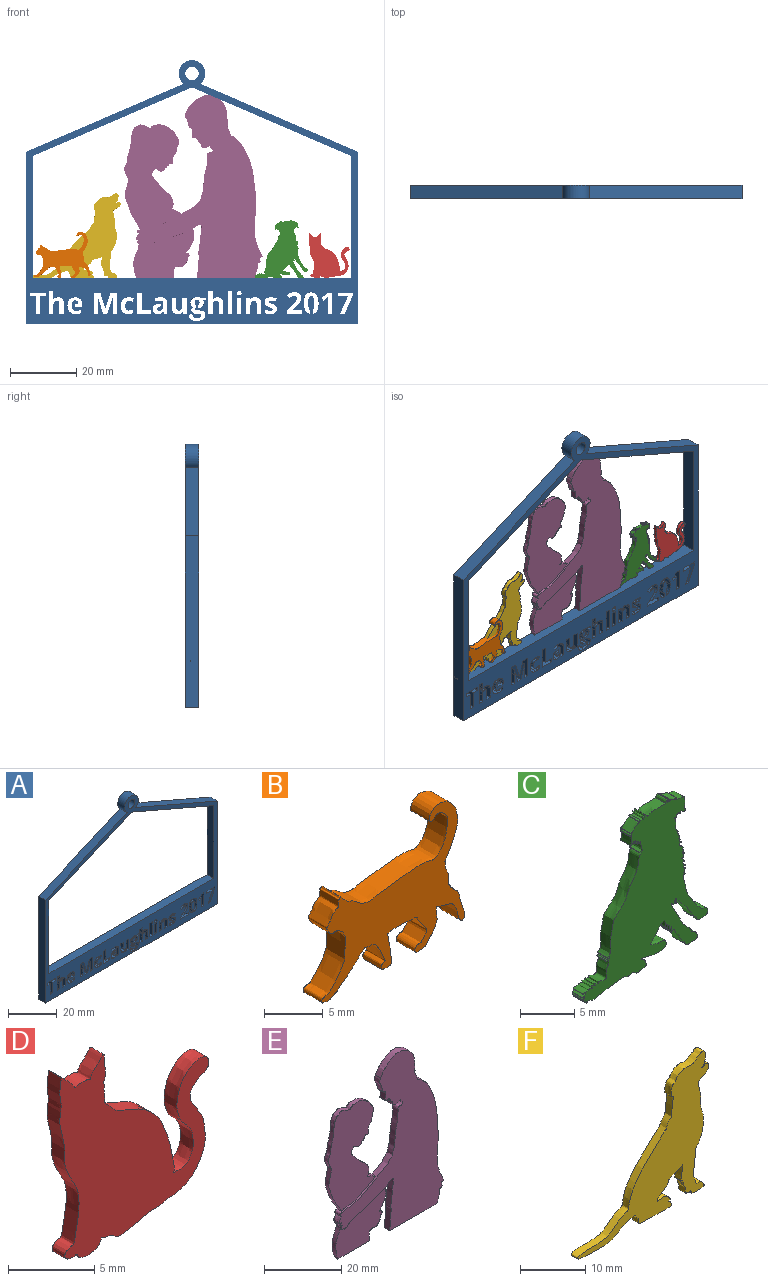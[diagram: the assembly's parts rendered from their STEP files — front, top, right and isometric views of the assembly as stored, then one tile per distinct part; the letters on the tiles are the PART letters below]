
ASSEMBLY  parts=6 mates=6
PART A: 327 faces, bbox 100x4x79.4 mm
  f0: extruded ~4x1.22mm, area 5.9mm2, adj f7,f8,f241,f326
  f1: extruded ~4x1.27mm, area 5.5mm2, adj f7,f8,f250,f316
  f2: plane 4x0.02mm, normal (0.11,0,0.99), area 0.1mm2, adj f7,f8,f251,f315
  f3: extruded ~4x0.02mm, area 0.1mm2, adj f7,f8,f261,f307
  f4: extruded ~4x0.17mm, area 0.9mm2, adj f7,f8,f260,f308
  f5: plane 4x0.02mm, normal (0.03,0,-1), area 0.1mm2, adj f7,f8,f133,f296
  f6: plane 4x2.38mm, normal (0,0,1), area 9.5mm2, adj f7,f8,f114,f287
  f7: plane 100x79.38mm, normal (0,-1,0), area 1515.6mm2, adj f0,f1,f2,f3,f4,f5,f6,f9
  f8: plane 100x79.38mm, normal (0,1,0), area 1515.6mm2, adj f0,f1,f2,f3,f4,f5,f6,f9
  f9: plane 36.69x4mm, normal (-1,0,0), area 146.7mm2, adj f7,f8,f10,f19
  f10: plane 96x4mm, normal (0,0,1), area 384mm2, adj f7,f8,f9,f11
  f11: plane 36.69x4mm, normal (1,0,0), area 146.7mm2, adj f7,f8,f10,f12
  f12: plane 48x20.72mm, normal (0.4,0,-0.92), area 209.1mm2, adj f7,f8,f11,f19
  f13: plane 47.47x20.48mm, normal (0.4,0,0.92), area 206.8mm2, adj f7,f8,f14,f18
  f14: cylinder r=4mm len=8mm, axis (0,1,0), area 78.6mm2, adj f7,f8,f13,f15
  f15: plane 47.47x20.48mm, normal (-0.4,0,0.92), area 206.8mm2, adj f7,f8,f14,f16
  f16: plane 51.8x4mm, normal (-1,0,0), area 207.2mm2, adj f7,f8,f15,f20
  f17: cylinder r=2mm len=4mm, axis (0,1,0), area 50.3mm2, adj f7,f8
  f18: plane 51.8x4mm, normal (1,0,0), area 207.2mm2, adj f7,f8,f13,f20
  f19: plane 48x20.72mm, normal (-0.4,0,-0.92), area 209.1mm2, adj f7,f8,f9,f12
  f20: plane 100x4mm, normal (0,0,-1), area 400mm2, adj f7,f8,f16,f18
  f21: plane 4x1.33mm, normal (0,0,1), area 5.3mm2, adj f7,f8,f22,f24
  f22: plane 4.89x4mm, normal (-1,0,0), area 19.6mm2, adj f7,f8,f21,f23
  f23: plane 4x1.33mm, normal (0,0,-1), area 5.3mm2, adj f7,f8,f22,f24
  f24: plane 4.89x4mm, normal (1,0,0), area 19.6mm2, adj f7,f8,f21,f23
  f25: plane 4x1.33mm, normal (0,0,1), area 5.3mm2, adj f7,f8,f26,f41
  f26: plane 4x3.19mm, normal (-1,0,0), area 12.8mm2, adj f7,f8,f25,f27
  f27: extruded ~4x1.33mm, area 5.8mm2, adj f7,f8,f26,f28
  f28: extruded ~4x1.3mm, area 5.7mm2, adj f7,f8,f27,f29
  f29: extruded ~4x0.89mm, area 3.7mm2, adj f7,f8,f28,f30
  f30: extruded ~4x0.62mm, area 3.3mm2, adj f7,f8,f29,f31
  f31: plane 4x0.07mm, normal (0,0,-1), area 0.3mm2, adj f7,f8,f30,f32
  f32: plane 4x0.63mm, normal (-0.96,0,-0.28), area 2.6mm2, adj f7,f8,f31,f33
  f33: plane 4x1.02mm, normal (0,0,-1), area 4.1mm2, adj f7,f8,f32,f34
  f34: plane 4.89x4mm, normal (1,0,0), area 19.6mm2, adj f7,f8,f33,f35
  f35: plane 4x1.33mm, normal (0,0,1), area 5.3mm2, adj f7,f8,f34,f36
  f36: plane 4x2.3mm, normal (-1,0,0), area 9.2mm2, adj f7,f8,f35,f37
  f37: extruded ~4x1.24mm, area 5.1mm2, adj f7,f8,f36,f38
  f38: extruded ~4x0.81mm, area 3.7mm2, adj f7,f8,f37,f39
  f39: extruded ~4x0.6mm, area 2.7mm2, adj f7,f8,f38,f40
  f40: extruded ~4x0.79mm, area 3.3mm2, adj f7,f8,f39,f41
  f41: plane 4x2.86mm, normal (1,0,0), area 11.4mm2, adj f7,f8,f25,f40
  f42: extruded ~4x1.15mm, area 5.2mm2, adj f7,f8,f43,f67
  f43: extruded ~4x0.63mm, area 2.6mm2, adj f7,f8,f42,f44
  f44: extruded ~4x0.46mm, area 2.5mm2, adj f7,f8,f43,f45
  f45: extruded ~4x0.84mm, area 3.8mm2, adj f7,f8,f44,f46
  f46: extruded ~4x0.83mm, area 3.7mm2, adj f7,f8,f45,f47
  f47: extruded ~4x0.31mm, area 1.5mm2, adj f7,f8,f46,f48
  f48: extruded ~4x0.59mm, area 3mm2, adj f7,f8,f47,f49
  f49: extruded ~4x0.65mm, area 2.7mm2, adj f7,f8,f48,f50
  f50: extruded ~4x0.69mm, area 2.9mm2, adj f7,f8,f49,f51
  f51: plane 4x0.96mm, normal (-0.92,0,0.39), area 4.2mm2, adj f7,f8,f50,f52
  f52: extruded ~4x1.72mm, area 7.1mm2, adj f7,f8,f51,f53
  f53: extruded ~4x1.43mm, area 6mm2, adj f7,f8,f52,f54
  f54: extruded ~4x1.01mm, area 4.7mm2, adj f7,f8,f53,f55
  f55: extruded ~4x0.64mm, area 2.6mm2, adj f7,f8,f54,f56
  f56: extruded ~4x0.46mm, area 2.4mm2, adj f7,f8,f55,f57
  f57: extruded ~4x0.83mm, area 3.8mm2, adj f7,f8,f56,f58
  f58: extruded ~4x0.63mm, area 2.8mm2, adj f7,f8,f57,f59
  f59: extruded ~4x0.33mm, area 1.6mm2, adj f7,f8,f58,f60
  f60: extruded ~4x0.26mm, area 1.1mm2, adj f7,f8,f59,f61
  f61: extruded ~4x0.73mm, area 3.8mm2, adj f7,f8,f60,f62
  f62: extruded ~4x0.82mm, area 3.3mm2, adj f7,f8,f61,f63
  f63: extruded ~4x0.84mm, area 3.6mm2, adj f7,f8,f62,f64
  f64: plane 4x1.1mm, normal (1,0,0), area 4.4mm2, adj f7,f8,f63,f65
  f65: extruded ~4x0.7mm, area 2.9mm2, adj f7,f8,f64,f66
  f66: extruded ~4x0.91mm, area 3.7mm2, adj f7,f8,f65,f67
  f67: extruded ~4x1.57mm, area 6.6mm2, adj f7,f8,f42,f66
  f68: plane 4.47x4mm, normal (0,0,1), area 17.9mm2, adj f7,f8,f69,f91
  f69: plane 4x1.14mm, normal (-1,0,0), area 4.6mm2, adj f7,f8,f68,f70
  f70: plane 4x2.79mm, normal (0,0,-1), area 11.2mm2, adj f7,f8,f69,f71
  f71: plane 4x0.06mm, normal (-1,0,0), area 0.2mm2, adj f7,f8,f70,f72
  f72: plane 4x0.82mm, normal (-0.69,0,0.73), area 4.5mm2, adj f7,f8,f71,f73
  f73: extruded ~4x1.16mm, area 6.5mm2, adj f7,f8,f72,f74
  f74: extruded ~4x0.79mm, area 3.7mm2, adj f7,f8,f73,f75
  f75: extruded ~4x0.83mm, area 3.4mm2, adj f7,f8,f74,f76
  f76: extruded ~4x0.9mm, area 3.8mm2, adj f7,f8,f75,f77
  f77: extruded ~4x0.71mm, area 3.8mm2, adj f7,f8,f76,f78
  f78: extruded ~4x1.06mm, area 4.4mm2, adj f7,f8,f77,f79
  f79: extruded ~4x0.82mm, area 3.3mm2, adj f7,f8,f78,f80
  f80: extruded ~4x0.68mm, area 2.9mm2, adj f7,f8,f79,f81
  f81: extruded ~4x0.78mm, area 3.9mm2, adj f7,f8,f80,f82
  f82: plane 4x0.87mm, normal (0.76,0,0.65), area 4.6mm2, adj f7,f8,f81,f83
  f83: extruded ~4x0.73mm, area 3.5mm2, adj f7,f8,f82,f84
  f84: extruded ~4x0.72mm, area 3mm2, adj f7,f8,f83,f85
  f85: extruded ~4x0.57mm, area 2.4mm2, adj f7,f8,f84,f86
  f86: extruded ~4x0.57mm, area 2.5mm2, adj f7,f8,f85,f87
  f87: extruded ~4x0.5mm, area 2mm2, adj f7,f8,f86,f88
  f88: extruded ~4x0.52mm, area 2.5mm2, adj f7,f8,f87,f89
  f89: extruded ~4x1.01mm, area 5.5mm2, adj f7,f8,f88,f90
  f90: plane 4x1.62mm, normal (0.71,0,-0.7), area 9.1mm2, adj f7,f8,f89,f91
  f91: plane 4x0.94mm, normal (1,0,0), area 3.8mm2, adj f7,f8,f68,f90
  f92: plane 4x1.35mm, normal (0,0,1), area 5.4mm2, adj f7,f8,f93,f101
  f93: plane 6.4x4mm, normal (-1,0,0), area 25.6mm2, adj f7,f8,f92,f94
  f94: plane 4x1.11mm, normal (0,0,-1), area 4.4mm2, adj f7,f8,f93,f95
  f95: plane 4x2.06mm, normal (0.62,0,-0.78), area 10.5mm2, adj f7,f8,f94,f96
  f96: plane 4x0.81mm, normal (0.78,0,0.63), area 4.2mm2, adj f7,f8,f95,f97
  f97: plane 4x0.74mm, normal (-0.63,0,0.78), area 3.8mm2, adj f7,f8,f96,f98
  f98: extruded ~4x0.47mm, area 2.6mm2, adj f7,f8,f97,f99
  f99: plane 4x0.67mm, normal (1,0,-0.03), area 2.7mm2, adj f7,f8,f98,f100
  f100: plane 4x0.61mm, normal (1,0,-0.02), area 2.4mm2, adj f7,f8,f99,f101
  f101: plane 4x3.7mm, normal (1,0,0), area 14.8mm2, adj f7,f8,f92,f100
  f102: plane 5.25x4mm, normal (0.91,0,-0.42), area 23.1mm2, adj f7,f8,f103,f108
  f103: plane 4x1.42mm, normal (0,0,1), area 5.7mm2, adj f7,f8,f102,f104
  f104: plane 5.54x4mm, normal (-0.92,0,0.4), area 24.2mm2, adj f7,f8,f103,f105
  f105: plane 4x0.85mm, normal (-1,0,0), area 3.4mm2, adj f7,f8,f104,f106
  f106: plane 4.59x4mm, normal (0,0,-1), area 18.4mm2, adj f7,f8,f105,f107
  f107: plane 4x1.14mm, normal (1,0,0), area 4.6mm2, adj f7,f8,f106,f108
  f108: plane 4x3.16mm, normal (0,0,1), area 12.6mm2, adj f7,f8,f102,f107
  f109: extruded ~4x1.85mm, area 8.1mm2, adj f7,f8,f110,f123
  f110: extruded ~4x1.9mm, area 8.2mm2, adj f7,f8,f109,f111
  f111: extruded ~4x1.7mm, area 7.5mm2, adj f7,f8,f110,f112
  f112: extruded ~4x1.61mm, area 7.1mm2, adj f7,f8,f111,f113
  f113: extruded ~4x1.63mm, area 7.1mm2, adj f7,f8,f112,f114
  f114: plane 4x0.65mm, normal (-1,0,0), area 2.6mm2, adj f6,f7,f8,f113
  f115: plane 4x0.07mm, normal (0,0,1), area 0.3mm2, adj f7,f8,f116,f288
  f116: extruded ~4x0.89mm, area 3.9mm2, adj f7,f8,f115,f117
  f117: extruded ~4x0.88mm, area 3.9mm2, adj f7,f8,f116,f118
  f118: extruded ~4x0.84mm, area 3.4mm2, adj f7,f8,f117,f119
  f119: extruded ~4x0.82mm, area 3.5mm2, adj f7,f8,f118,f120
  f120: plane 4x1.03mm, normal (-1,0,0), area 4.1mm2, adj f7,f8,f119,f121
  f121: extruded ~4x0.75mm, area 3.2mm2, adj f7,f8,f120,f122
  f122: extruded ~4x0.97mm, area 3.9mm2, adj f7,f8,f121,f123
  f123: extruded ~4x1.85mm, area 8mm2, adj f7,f8,f109,f122
  f124: plane 4x0.67mm, normal (0.93,0,0.36), area 2.9mm2, adj f7,f8,f125,f141
  f125: plane 4x0.93mm, normal (0,0,1), area 3.7mm2, adj f7,f8,f124,f126
  f126: plane 4x3.26mm, normal (-1,0,0), area 13mm2, adj f7,f8,f125,f127
  f127: extruded ~4x1.3mm, area 5.8mm2, adj f7,f8,f126,f128
  f128: extruded ~4x1.51mm, area 6.4mm2, adj f7,f8,f127,f129
  f129: extruded ~4x1.87mm, area 7.8mm2, adj f7,f8,f128,f130
  f130: plane 4x0.9mm, normal (0.9,0,0.44), area 4mm2, adj f7,f8,f129,f131
  f131: extruded ~4x1.38mm, area 5.7mm2, adj f7,f8,f130,f132
  f132: extruded ~4x0.76mm, area 4.9mm2, adj f7,f8,f131,f133
  f133: plane 4x0.21mm, normal (1,0,0), area 0.9mm2, adj f5,f7,f8,f132
  f134: plane 4x0.25mm, normal (0.03,0,-1), area 1mm2, adj f7,f8,f135,f297
  f135: extruded ~4x1.64mm, area 6.9mm2, adj f7,f8,f134,f136
  f136: extruded ~4x1.15mm, area 5.3mm2, adj f7,f8,f135,f137
  f137: extruded ~4x1.15mm, area 5mm2, adj f7,f8,f136,f138
  f138: extruded ~4x1.11mm, area 4.9mm2, adj f7,f8,f137,f139
  f139: extruded ~4x0.93mm, area 3.8mm2, adj f7,f8,f138,f140
  f140: extruded ~4x0.69mm, area 3.7mm2, adj f7,f8,f139,f141
  f141: plane 4x0.04mm, normal (0,0,1), area 0.1mm2, adj f7,f8,f124,f140
  f142: extruded ~4x0.73mm, area 4.5mm2, adj f7,f8,f143,f146
  f143: extruded ~4x0.73mm, area 4.5mm2, adj f7,f8,f142,f144
  f144: extruded ~4x0.55mm, area 2.3mm2, adj f7,f8,f143,f145
  f145: extruded ~4x0.48mm, area 2.1mm2, adj f7,f8,f144,f146
  f146: extruded ~4x0.73mm, area 4.5mm2, adj f7,f8,f142,f145
  f147: plane 4x1.33mm, normal (0,0,1), area 5.3mm2, adj f7,f8,f148,f150
  f148: plane 6.81x4mm, normal (-1,0,0), area 27.2mm2, adj f7,f8,f147,f149
  f149: plane 4x1.33mm, normal (0,0,-1), area 5.3mm2, adj f7,f8,f148,f150
  f150: plane 6.81x4mm, normal (1,0,0), area 27.2mm2, adj f7,f8,f147,f149
  f151: plane 4x1.33mm, normal (0,0,1), area 5.3mm2, adj f7,f8,f152,f167
  f152: plane 4x3.19mm, normal (-1,0,0), area 12.8mm2, adj f7,f8,f151,f153
  f153: extruded ~4x1.33mm, area 5.8mm2, adj f7,f8,f152,f154
  f154: extruded ~4x1.31mm, area 5.7mm2, adj f7,f8,f153,f155
  f155: extruded ~4x1.42mm, area 6.7mm2, adj f7,f8,f154,f156
  f156: plane 4x0.07mm, normal (0,0,-1), area 0.3mm2, adj f7,f8,f155,f157
  f157: plane 4x0.39mm, normal (-1,0,0.08), area 1.6mm2, adj f7,f8,f156,f158
  f158: extruded ~4x0.76mm, area 3.1mm2, adj f7,f8,f157,f159
  f159: plane 4x1.39mm, normal (-1,0,0), area 5.6mm2, adj f7,f8,f158,f160
  f160: plane 4x1.33mm, normal (0,0,-1), area 5.3mm2, adj f7,f8,f159,f161
  f161: plane 6.81x4mm, normal (1,0,0), area 27.2mm2, adj f7,f8,f160,f162
  f162: plane 4x1.33mm, normal (0,0,1), area 5.3mm2, adj f7,f8,f161,f163
  f163: plane 4x2.3mm, normal (-1,0,0), area 9.2mm2, adj f7,f8,f162,f164
  f164: extruded ~4x1.23mm, area 5.1mm2, adj f7,f8,f163,f165
  f165: extruded ~4x0.81mm, area 3.7mm2, adj f7,f8,f164,f166
  f166: extruded ~4x1.06mm, area 6mm2, adj f7,f8,f165,f167
  f167: plane 4x2.86mm, normal (1,0,0), area 11.4mm2, adj f7,f8,f151,f166
  f168: plane 4x0.63mm, normal (0.96,0,0.28), area 2.6mm2, adj f7,f8,f169,f184
  f169: plane 4x1.02mm, normal (0,0,1), area 4.1mm2, adj f7,f8,f168,f170
  f170: plane 4.89x4mm, normal (-1,0,0), area 19.6mm2, adj f7,f8,f169,f171
  f171: plane 4x1.33mm, normal (0,0,-1), area 5.3mm2, adj f7,f8,f170,f172
  f172: plane 4x2.3mm, normal (1,0,0), area 9.2mm2, adj f7,f8,f171,f173
  f173: extruded ~4x1.24mm, area 5.1mm2, adj f7,f8,f172,f174
  f174: extruded ~4x0.81mm, area 3.7mm2, adj f7,f8,f173,f175
  f175: extruded ~4x0.6mm, area 2.7mm2, adj f7,f8,f174,f176
  f176: extruded ~4x0.79mm, area 3.3mm2, adj f7,f8,f175,f177
  f177: plane 4x2.86mm, normal (-1,0,0), area 11.4mm2, adj f7,f8,f176,f178
  f178: plane 4x1.33mm, normal (0,0,-1), area 5.3mm2, adj f7,f8,f177,f179
  f179: plane 4x3.19mm, normal (1,0,0), area 12.8mm2, adj f7,f8,f178,f180
  f180: extruded ~4x1.33mm, area 5.7mm2, adj f7,f8,f179,f181
  f181: extruded ~4x1.3mm, area 5.7mm2, adj f7,f8,f180,f182
  f182: extruded ~4x0.9mm, area 3.7mm2, adj f7,f8,f181,f183
  f183: extruded ~4x0.61mm, area 3.3mm2, adj f7,f8,f182,f184
  f184: plane 4x0.07mm, normal (0,0,1), area 0.3mm2, adj f7,f8,f168,f183
  f185: plane 6.4x4mm, normal (1,0,0), area 25.6mm2, adj f7,f8,f186,f190
  f186: plane 4x3.95mm, normal (0,0,1), area 15.8mm2, adj f7,f8,f185,f187
  f187: plane 4x1.12mm, normal (-1,0,0), area 4.5mm2, adj f7,f8,f186,f188
  f188: plane 4x2.6mm, normal (0,0,-1), area 10.4mm2, adj f7,f8,f187,f189
  f189: plane 5.28x4mm, normal (-1,0,0), area 21.1mm2, adj f7,f8,f188,f190
  f190: plane 4x1.36mm, normal (0,0,-1), area 5.4mm2, adj f7,f8,f185,f189
  f191: extruded ~4x2.51mm, area 15.6mm2, adj f7,f8,f192,f204
  f192: extruded ~4x0.83mm, area 3.4mm2, adj f7,f8,f191,f193
  f193: extruded ~4x0.65mm, area 2.9mm2, adj f7,f8,f192,f194
  f194: plane 4x1.14mm, normal (-1,0,0), area 4.6mm2, adj f7,f8,f193,f195
  f195: extruded ~4x0.66mm, area 2.9mm2, adj f7,f8,f194,f196
  f196: extruded ~4x0.71mm, area 2.9mm2, adj f7,f8,f195,f197
  f197: extruded ~4x1.44mm, area 8.1mm2, adj f7,f8,f196,f198
  f198: extruded ~4x1.48mm, area 8.2mm2, adj f7,f8,f197,f199
  f199: extruded ~4x0.54mm, area 2.2mm2, adj f7,f8,f198,f200
  f200: extruded ~4x0.59mm, area 2.5mm2, adj f7,f8,f199,f201
  f201: plane 4x1.03mm, normal (-0.93,0,0.36), area 4.4mm2, adj f7,f8,f200,f202
  f202: extruded ~4x1.52mm, area 6.3mm2, adj f7,f8,f201,f203
  f203: extruded ~4x1.78mm, area 7.8mm2, adj f7,f8,f202,f204
  f204: extruded ~4x1.91mm, area 8.2mm2, adj f7,f8,f191,f203
  f205: plane 5.02x4mm, normal (0.96,0,0.29), area 21mm2, adj f7,f8,f206,f223
  f206: plane 4x1.24mm, normal (0,0,1), area 5mm2, adj f7,f8,f205,f207
  f207: plane 5.01x4mm, normal (-0.95,0,0.31), area 21.1mm2, adj f7,f8,f206,f208
  f208: plane 4x0.04mm, normal (0,0,1), area 0.2mm2, adj f7,f8,f207,f209
  f209: extruded ~4x1.49mm, area 6mm2, adj f7,f8,f208,f210
  f210: extruded ~4x0.49mm, area 2mm2, adj f7,f8,f209,f211
  f211: plane 4x3.03mm, normal (1,0,0), area 12.1mm2, adj f7,f8,f210,f212
  f212: plane 4x1.26mm, normal (0,0,1), area 5.1mm2, adj f7,f8,f211,f213
  f213: plane 6.4x4mm, normal (-1,0,0), area 25.6mm2, adj f7,f8,f212,f214
  f214: plane 4x1.85mm, normal (0,0,-1), area 7.4mm2, adj f7,f8,f213,f215
  f215: plane 4.89x4mm, normal (0.95,0,-0.31), area 20.6mm2, adj f7,f8,f214,f216
  f216: plane 4x0.03mm, normal (0,0,-1), area 0.1mm2, adj f7,f8,f215,f217
  f217: plane 4.89x4mm, normal (-0.96,0,-0.3), area 20.5mm2, adj f7,f8,f216,f218
  f218: plane 4x1.85mm, normal (0,0,-1), area 7.4mm2, adj f7,f8,f217,f219
  f219: plane 6.4x4mm, normal (1,0,0), area 25.6mm2, adj f7,f8,f218,f220
  f220: plane 4x1.21mm, normal (0,0,1), area 4.9mm2, adj f7,f8,f219,f221
  f221: plane 4x2.98mm, normal (-1,0,0), area 11.9mm2, adj f7,f8,f220,f222
  f222: extruded ~4x2.04mm, area 8.2mm2, adj f7,f8,f221,f223
  f223: plane 4x0.04mm, normal (0,0,1), area 0.2mm2, adj f7,f8,f205,f222
  f224: plane 4x1.33mm, normal (0,0,1), area 5.3mm2, adj f7,f8,f225,f240
  f225: plane 4x3.19mm, normal (-1,0,0), area 12.8mm2, adj f7,f8,f224,f226
  f226: extruded ~4x1.33mm, area 5.8mm2, adj f7,f8,f225,f227
  f227: extruded ~4x1.31mm, area 5.7mm2, adj f7,f8,f226,f228
  f228: extruded ~4x1.42mm, area 6.7mm2, adj f7,f8,f227,f229
  f229: plane 4x0.07mm, normal (0,0,-1), area 0.3mm2, adj f7,f8,f228,f230
  f230: plane 4x0.39mm, normal (-1,0,0.08), area 1.6mm2, adj f7,f8,f229,f231
  f231: extruded ~4x0.76mm, area 3.1mm2, adj f7,f8,f230,f232
  f232: plane 4x1.39mm, normal (-1,0,0), area 5.6mm2, adj f7,f8,f231,f233
  f233: plane 4x1.33mm, normal (0,0,-1), area 5.3mm2, adj f7,f8,f232,f234
  f234: plane 6.81x4mm, normal (1,0,0), area 27.2mm2, adj f7,f8,f233,f235
  f235: plane 4x1.33mm, normal (0,0,1), area 5.3mm2, adj f7,f8,f234,f236
  f236: plane 4x2.3mm, normal (-1,0,0), area 9.2mm2, adj f7,f8,f235,f237
  f237: extruded ~4x1.23mm, area 5.1mm2, adj f7,f8,f236,f238
  f238: extruded ~4x0.81mm, area 3.7mm2, adj f7,f8,f237,f239
  f239: extruded ~4x1.06mm, area 6mm2, adj f7,f8,f238,f240
  f240: plane 4x2.86mm, normal (1,0,0), area 11.4mm2, adj f7,f8,f224,f239
  f241: extruded ~4x2.48mm, area 10.3mm2, adj f0,f7,f8,f242
  f242: extruded ~4x2.46mm, area 10.2mm2, adj f7,f8,f241,f243
  f243: extruded ~4x1.67mm, area 7.8mm2, adj f7,f8,f242,f244
  f244: extruded ~4x1.69mm, area 7.8mm2, adj f7,f8,f243,f245
  f245: extruded ~4x2.5mm, area 10.4mm2, adj f7,f8,f244,f246
  f246: extruded ~4x2.46mm, area 10.2mm2, adj f7,f8,f245,f247
  f247: extruded ~4x1.29mm, area 6.3mm2, adj f7,f8,f246,f325
  f248: plane 4x0.77mm, normal (-0.25,0,0.97), area 3.2mm2, adj f7,f8,f249,f272
  f249: extruded ~4x0.74mm, area 3.1mm2, adj f7,f8,f248,f250
  f250: extruded ~4x1.23mm, area 5.6mm2, adj f1,f7,f8,f249
  f251: extruded ~4x0.35mm, area 1.7mm2, adj f2,f7,f8,f252
  f252: extruded ~4x0.74mm, area 3.5mm2, adj f7,f8,f251,f253
  f253: plane 4x0.83mm, normal (0,0,-1), area 3.3mm2, adj f7,f8,f252,f254
  f254: extruded ~4x1.23mm, area 5.2mm2, adj f7,f8,f253,f255
  f255: extruded ~4x1.02mm, area 4.6mm2, adj f7,f8,f254,f256
  f256: extruded ~4x1.33mm, area 6.3mm2, adj f7,f8,f255,f257
  f257: extruded ~4x2.05mm, area 8.5mm2, adj f7,f8,f256,f258
  f258: extruded ~4x1.56mm, area 6.5mm2, adj f7,f8,f257,f259
  f259: extruded ~4x1mm, area 4.8mm2, adj f7,f8,f258,f260
  f260: extruded ~4x0.74mm, area 3.2mm2, adj f4,f7,f8,f259
  f261: extruded ~4x0.36mm, area 1.9mm2, adj f3,f7,f8,f262
  f262: extruded ~4x0.42mm, area 1.8mm2, adj f7,f8,f261,f263
  f263: extruded ~4x0.47mm, area 2mm2, adj f7,f8,f262,f264
  f264: extruded ~4x0.47mm, area 2.4mm2, adj f7,f8,f263,f265
  f265: extruded ~4x0.61mm, area 3.3mm2, adj f7,f8,f264,f266
  f266: extruded ~4x0.87mm, area 3.6mm2, adj f7,f8,f265,f267
  f267: extruded ~4x1.24mm, area 5.6mm2, adj f7,f8,f266,f268
  f268: extruded ~4x1.49mm, area 6.3mm2, adj f7,f8,f267,f269
  f269: extruded ~4x0.49mm, area 2mm2, adj f7,f8,f268,f270
  f270: extruded ~4x0.36mm, area 1.5mm2, adj f7,f8,f269,f271
  f271: plane 4x1.71mm, normal (0,0,-1), area 6.8mm2, adj f7,f8,f270,f272
  f272: plane 4x0.68mm, normal (-1,0,0), area 2.7mm2, adj f7,f8,f248,f271
  f273: plane 4x1.36mm, normal (0,0,1), area 5.4mm2, adj f7,f8,f274,f280
  f274: plane 5.27x4mm, normal (-1,0,0), area 21.1mm2, adj f7,f8,f273,f275
  f275: plane 4x1.74mm, normal (0,0,1), area 6.9mm2, adj f7,f8,f274,f276
  f276: plane 4x1.13mm, normal (-1,0,0), area 4.5mm2, adj f7,f8,f275,f277
  f277: plane 4.83x4mm, normal (0,0,-1), area 19.3mm2, adj f7,f8,f276,f278
  f278: plane 4x1.13mm, normal (1,0,0), area 4.5mm2, adj f7,f8,f277,f279
  f279: plane 4x1.74mm, normal (0,0,1), area 7mm2, adj f7,f8,f278,f280
  f280: plane 5.27x4mm, normal (1,0,0), area 21.1mm2, adj f7,f8,f273,f279
  f281: plane 4x1.13mm, normal (0,0,-1), area 4.5mm2, adj f7,f8,f284,f287
  f282: extruded ~4x0.67mm, area 3mm2, adj f7,f8,f283,f286
  f283: extruded ~4x0.67mm, area 3mm2, adj f7,f8,f282,f284
  f284: extruded ~4x0.76mm, area 3.3mm2, adj f7,f8,f281,f283
  f285: plane 4x0.04mm, normal (0,0,-1), area 0.2mm2, adj f7,f8,f286,f288
  f286: extruded ~4x0.76mm, area 3.3mm2, adj f7,f8,f282,f285
  f287: plane 4x0.89mm, normal (1,0,0), area 3.6mm2, adj f6,f7,f8,f281
  f288: plane 4x0.89mm, normal (-1,0,0), area 3.6mm2, adj f7,f8,f115,f285
  f289: extruded ~4x0.81mm, area 3.4mm2, adj f7,f8,f290,f297
  f290: extruded ~4x0.59mm, area 2.7mm2, adj f7,f8,f289,f291
  f291: extruded ~4x0.65mm, area 3.9mm2, adj f7,f8,f290,f292
  f292: extruded ~4x0.74mm, area 3.2mm2, adj f7,f8,f291,f293
  f293: extruded ~4x0.71mm, area 3.1mm2, adj f7,f8,f292,f294
  f294: plane 4x0.4mm, normal (1,0,0), area 1.6mm2, adj f7,f8,f293,f295
  f295: plane 4x0.02mm, normal (-0.04,0,1), area 0.1mm2, adj f7,f8,f294,f296
  f296: plane 4x0.78mm, normal (1,0,0), area 3.1mm2, adj f5,f7,f8,f295
  f297: plane 4x0.78mm, normal (-1,0,-0.03), area 3.1mm2, adj f7,f8,f134,f289
  f298: extruded ~4x0.08mm, area 0.3mm2, adj f7,f8,f300,f308
  f299: extruded ~4x0.35mm, area 1.4mm2, adj f7,f8,f301,f307
  f300: extruded ~4x0.43mm, area 2.1mm2, adj f7,f8,f298,f306
  f301: plane 4x0.69mm, normal (0,0,1), area 2.8mm2, adj f7,f8,f299,f302
  f302: extruded ~4x0.74mm, area 3mm2, adj f7,f8,f301,f303
  f303: extruded ~4x0.38mm, area 1.9mm2, adj f7,f8,f302,f304
  f304: extruded ~4x0.54mm, area 2.9mm2, adj f7,f8,f303,f305
  f305: extruded ~4x1.12mm, area 4.6mm2, adj f7,f8,f304,f306
  f306: extruded ~4x0.74mm, area 3.1mm2, adj f7,f8,f300,f305
  f307: plane 4x0.59mm, normal (0.62,0,0.78), area 3mm2, adj f3,f7,f8,f299
  f308: plane 4x0.72mm, normal (-0.7,0,-0.72), area 4mm2, adj f4,f7,f8,f298
  f309: extruded ~4x0.2mm, area 1mm2, adj f7,f8,f314,f315
  f310: extruded ~4x0.37mm, area 1.8mm2, adj f7,f8,f311,f316
  f311: extruded ~4x0.63mm, area 2.7mm2, adj f7,f8,f310,f312
  f312: extruded ~4x0.88mm, area 5.2mm2, adj f7,f8,f311,f313
  f313: extruded ~4x0.88mm, area 5.3mm2, adj f7,f8,f312,f314
  f314: extruded ~4x0.63mm, area 2.7mm2, adj f7,f8,f309,f313
  f315: plane 4x0.85mm, normal (-0.99,0,0.16), area 3.5mm2, adj f2,f7,f8,f309
  f316: plane 4x0.82mm, normal (1,0,0), area 3.3mm2, adj f1,f7,f8,f310
  f317: extruded ~4x0.34mm, area 1.6mm2, adj f7,f8,f319,f326
  f318: extruded ~4x0.41mm, area 2.1mm2, adj f7,f8,f324,f325
  f319: extruded ~4x1.68mm, area 6.8mm2, adj f7,f8,f317,f320
  f320: extruded ~4x1.69mm, area 6.9mm2, adj f7,f8,f319,f321
  f321: extruded ~4x0.68mm, area 3.6mm2, adj f7,f8,f320,f322
  f322: extruded ~4x0.68mm, area 3.7mm2, adj f7,f8,f321,f323
  f323: extruded ~4x1.69mm, area 6.9mm2, adj f7,f8,f322,f324
  f324: extruded ~4x1.69mm, area 6.8mm2, adj f7,f8,f318,f323
  f325: plane 4x1.17mm, normal (-1,0,0), area 4.7mm2, adj f7,f8,f247,f318
  f326: plane 4x1.23mm, normal (1,0,0), area 4.9mm2, adj f0,f7,f8,f317
PART B: 4 faces, bbox 17.2x2.3x14.1 mm
  f0: extruded ~14.34x13.23mm, area 101.3mm2, adj f1,f2,f3
  f1: extruded ~13.84x10.12mm, area 104mm2, adj f0,f2,f3
  f2: plane 17.2x14.11mm, normal (0,-1,0), area 99.6mm2, adj f0,f1
  f3: plane 17.2x14.11mm, normal (0,1,0), area 99.6mm2, adj f0,f1
PART C: 9 faces, bbox 16.4x1.3x17.8 mm
  f0: extruded ~17.42x7.47mm, area 84.8mm2, adj f1,f6,f7,f8
  f1: extruded ~3.22x1.3mm, area 5.5mm2, adj f0,f2,f7,f8
  f2: extruded ~2.48x1.32mm, area 7.6mm2, adj f1,f3,f7,f8
  f3: extruded ~11.22x4.45mm, area 17.9mm2, adj f2,f4,f7,f8
  f4: extruded ~2.1x1.84mm, area 5.9mm2, adj f3,f5,f7,f8
  f5: extruded ~1.69x1.3mm, area 5.3mm2, adj f4,f6,f7,f8
  f6: extruded ~8.44x1.45mm, area 14.7mm2, adj f0,f5,f7,f8
  f7: plane 17.79x16.41mm, normal (0,-1,0), area 72.8mm2, adj f0,f1,f2,f3,f4,f5,f6
  f8: plane 17.79x16.41mm, normal (0,1,0), area 72.8mm2, adj f0,f1,f2,f3,f4,f5,f6
PART D: 3 faces, bbox 12.3x1.1x13.8 mm
  f0: extruded ~13.48x12mm, area 65.2mm2, adj f1,f2
  f1: plane 13.77x12.3mm, normal (0,-1,0), area 102.5mm2, adj f0
  f2: plane 13.77x12.3mm, normal (0,1,0), area 102.5mm2, adj f0
PART E: 15 faces, bbox 41.8x2x55.1 mm
  f0: extruded ~31.61x16.57mm, area 67.7mm2, adj f5,f6,f9,f12
  f1: extruded ~9.35x1.58mm, area 13.6mm2, adj f4,f7,f9,f12
  f2: extruded ~11.71x8.87mm, area 22.6mm2, adj f5,f8,f9,f12
  f3: extruded ~14.95x6.14mm, area 29mm2, adj f4,f7,f9,f12
  f4: plane 18.41x15.09mm, normal (0,-1,0), area 174.3mm2, adj f1,f3,f7,f12
  f5: plane 31.82x17.48mm, normal (0,-1,0), area 380.7mm2, adj f0,f2,f6,f8,f12
  f6: extruded ~8.1x7.63mm, area 20.5mm2, adj f0,f5,f8,f9
  f7: plane 11.62x1.4mm, normal (0,0,-1), area 16.3mm2, adj f1,f3,f4,f9
  f8: extruded ~1.4x0.46mm, area 0.7mm2, adj f2,f5,f6,f9
  f9: plane 55.06x41.79mm, normal (0,1,0), area 1465.7mm2, adj f0,f1,f2,f3,f6,f7,f8,f10
  f10: extruded ~55.05x22.87mm, area 147.9mm2, adj f9,f11,f13,f14
  f11: extruded ~9.92x4.7mm, area 24.1mm2, adj f9,f10,f12,f14
  f12: extruded ~40.27x22.77mm, area 115.7mm2, adj f0,f1,f2,f3,f4,f5,f9,f11
  f13: plane 17.33x1.96mm, normal (0,0,-1), area 34mm2, adj f9,f10,f12,f14
  f14: plane 55.06x38.32mm, normal (0,-1,0), area 936.4mm2, adj f10,f11,f12,f13
PART F: 3 faces, bbox 28.6x1.4x25.9 mm
  f0: extruded ~27.78x25.86mm, area 165.2mm2, adj f1,f2
  f1: plane 28.57x25.92mm, normal (0,-1,0), area 310.8mm2, adj f0
  f2: plane 28.57x25.92mm, normal (0,1,0), area 310.8mm2, adj f0
PLACE A t=(11.56,-25.03,29.92)mm
PLACE B t=(-1.93,-25.03,25.05)mm
PLACE C t=(57.67,-25.03,16.94)mm
PLACE D t=(65.31,-25.03,31.79)mm
PLACE E t=(31.55,-25.03,31.92)mm
PLACE F t=(4.37,-25.03,27.4)mm
MATE planar B.f3 <-> A.f8  axis (0,1,0) through (-27.01,-25.03,37.72)mm
MATE planar A.f8 <-> E.f9  axis (0,1,0) through (11.61,-25.03,36.88)mm
MATE planar A.f10 <-> E.f7  axis (0,0,1) through (11.56,-27.03,31.92)mm
MATE planar D.f2 <-> A.f8  axis (0,1,0) through (51.85,-25.03,37.38)mm
MATE planar C.f8 <-> A.f8  axis (0,1,0) through (39.09,-25.03,39.38)mm
MATE planar F.f2 <-> A.f8  axis (0,1,0) through (-18.5,-25.03,42.18)mm
